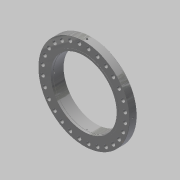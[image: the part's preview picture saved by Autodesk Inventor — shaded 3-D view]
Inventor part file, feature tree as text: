
AUTODESK INVENTOR PART (.ipt)
format: ipt  version: 2017.3 (Build 213257000, 257)  size: 383,488 bytes
history: native  units: in
note: dims shown in document units (in); Inventor stores cm internally (conversion verified against a paired STEP export)
features: sketch x6, hole x4, chamfer x4, extrude x3, pattern_circular x2, fillet x2, revolve x1, plane x1, projected_geometry x1
ambient origin geometry x8: Origin, YZ Plane, XZ Plane, XY Plane, X Axis, Y Axis, Z Axis, Center Point
bodies: Solid1 (feature_tree)
feature tree (24):
  extrude  "Extrusion1"  Depth=29.25in
  extrude  "Extrusion2"  Depth=31.5in
  extrude  "Extrusion3"  Depth=32.75in
  hole  "Hole1"  [1 undecoded]
  chamfer  "Chamfer3"  Distance=11.0236in Angle=360.0deg
  pattern_circular  "Circular Pattern1"  [2 undecoded]
  chamfer  "Chamfer2"  Distance=0.0312in Angle=45.0deg
  fillet  "Fillet2"  Radius=0.0625in
  chamfer  "Chamfer4"  Distance=0.2577in
  revolve  "Revolution1"  Angle=90.0deg
  fillet  "Fillet5"  Radius=0.25in
  chamfer  "Chamfer7"  Distance=0.6875in
  plane  "Work Plane1"
  sketch  "Sketch11"  dims[d25=0.0625in d26=0.125in d27=0.0687in d29=0.4375in d30=0.0312in d31=0.125in d32=45.0deg d33=0.0625in d34=0.125in d35=45.0deg d45=0.2577in d49=90.0deg d59=0.25in d69=0.6875in d70=0.125in d71=1.0in d72=14.75in d73=0.0312in d74=0.0312in d75=0.125in d76=45.0deg d96=16.0in d97=0.5in d98=1.0in d99=0.0442in d101=0.5in d102=0.688in d103=0.534in d104=0.0246in d105=0.688in d106=0.375in d107=0.25in d108=0.5635in d109=1.1in d110=0.8108in d111=0.417in d112=1.0in d113=0.375in d114=0.25in d115=0.5635in d116=1.75in d117=0.8108in d118=0.4062in d119=1.0in d120=0.375in d121=0.25in d122=0.5635in d123=6.0in d124=0.8108in d125=1.5748in d126=360.0deg]
  hole  "Hole4"  [1 undecoded]
  hole  "Hole5"  [1 undecoded]
  hole  "Hole6"  [1 undecoded]
  pattern_circular  "Circular Pattern3"  [2 undecoded]
  sketch  "Sketch1"  dims[d0=40.75in d1=29.25in]
  sketch  "Sketch2"  dims[d2=3.3125in d3=0.0in d4=31.5in]
  sketch  "Sketch3"  dims[d5=0.0625in d6=0.0in d7=32.75in]
  sketch  "Sketch4"  dims[d8=2.25in d9=0.0in d13=18.5in]
  sketch  "Sketch6"  dims[d15=1.75in d16=0.75in d17=0.375in d18=0.25in d19=0.5635in d20=1.0in d21=0.8108in d22=11.0236in d23=360.0deg]
  projected_geometry  "Projected Loop1"
note: 8 required parameter values undecoded (feature->parameter linkage not recoverable at this tier; creation-order binding heuristic only, values carry confidence <= 0.55)
